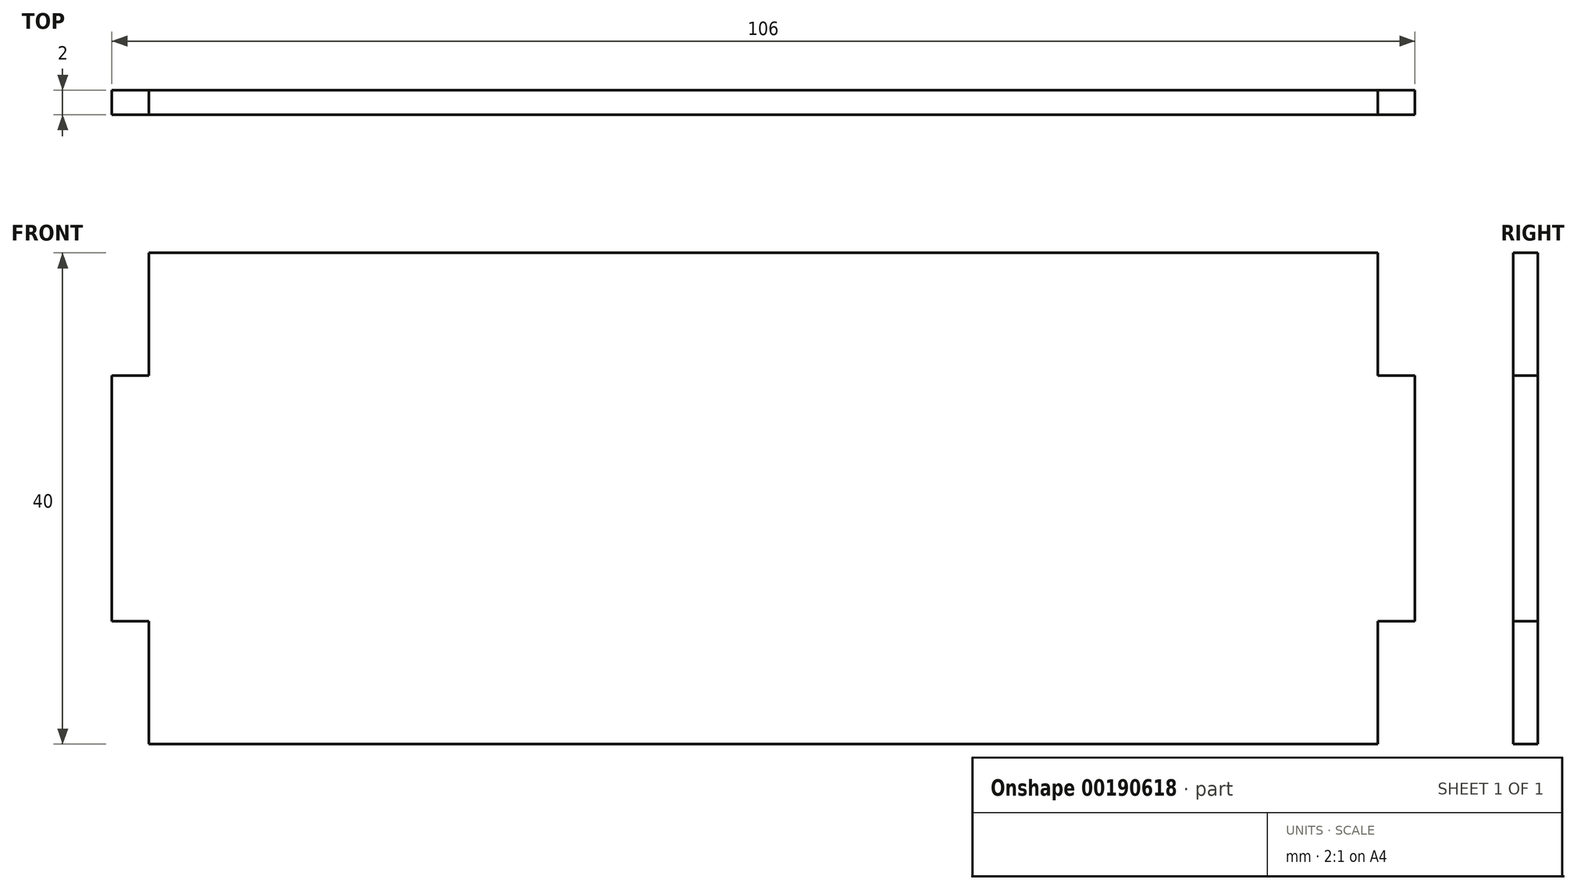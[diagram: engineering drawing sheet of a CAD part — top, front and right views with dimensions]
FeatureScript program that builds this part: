
annotation { "Feature Type Name" : "Feature", "Feature Type Description" : "" }
export const myFeature = defineFeature(function(context is Context, id is Id, definition is map)
    precondition{}
    {
        {
            var Q0;
            Q0=qCreatedBy(makeId("Front.planeOp"),FACE);
            var sketch = newSketch(context, id + "F0", { "sketchPlane" : qUnion([Q0])});
            skLineSegment(sketch, "E0.bottom", {"start": v(-50, 20) * mm, "end": v(50, 20) * mm});
            skLineSegment(sketch, "E0.top", {"start": v(-50, -20) * mm, "end": v(50, -20) * mm});
            skLineSegment(sketch, "E0.right", {"start": v(50, 20) * mm, "end": v(50, 10) * mm});
            skPoint(sketch, "E0.middle", {"position": v(0, 0) * mm});
            skLineSegment(sketch, "E1.bottom", {"start": v(50, 10) * mm, "end": v(53, 10) * mm});
            skLineSegment(sketch, "E1.top", {"start": v(50, -10) * mm, "end": v(53, -10) * mm});
            skLineSegment(sketch, "E1.right", {"start": v(53, 10) * mm, "end": v(53, -10) * mm});
            skLineSegment(sketch, "E2", {"start": v(152.85, 74.5) * mm, "end": v(152.85, 68.76) * mm});
            skLineSegment(sketch, "E3", {"start": v(0, 20) * mm, "end": v(0, -20) * mm, "construction": true});
            skLineSegment(sketch, "E4", {"start": v(50, -10) * mm, "end": v(50, -20) * mm});
            skLineSegment(sketch, "E5.MirrorCS", {"start": v(-50, 20) * mm, "end": v(-50, 10) * mm});
            skLineSegment(sketch, "E6.MirrorCS", {"start": v(-50, 10) * mm, "end": v(-53, 10) * mm});
            skLineSegment(sketch, "E7.MirrorCS", {"start": v(-53, 10) * mm, "end": v(-53, -10) * mm});
            skLineSegment(sketch, "E8.MirrorCS", {"start": v(-50, -10) * mm, "end": v(-53, -10) * mm});
            skLineSegment(sketch, "E9.MirrorCS", {"start": v(-50, -10) * mm, "end": v(-50, -20) * mm});
            skSolve(sketch);
        }
        {
            var Q0;
            Q0=makeQuery(id+"F0.imprint","IMPRINT",FACE,{"disambiguationData":[TD([[makeQuery(id+"F0.imprint","IMPRINT",EDGE,{"derivedFrom":sQuery(id+"F0.wireOp",EDGE,"E0.bottom")}),-1.0]])]});
            extrude(context, id + "F1", {"entities" : qUnion([Q0]), "depth" : 2 * mm});
        }
    });
